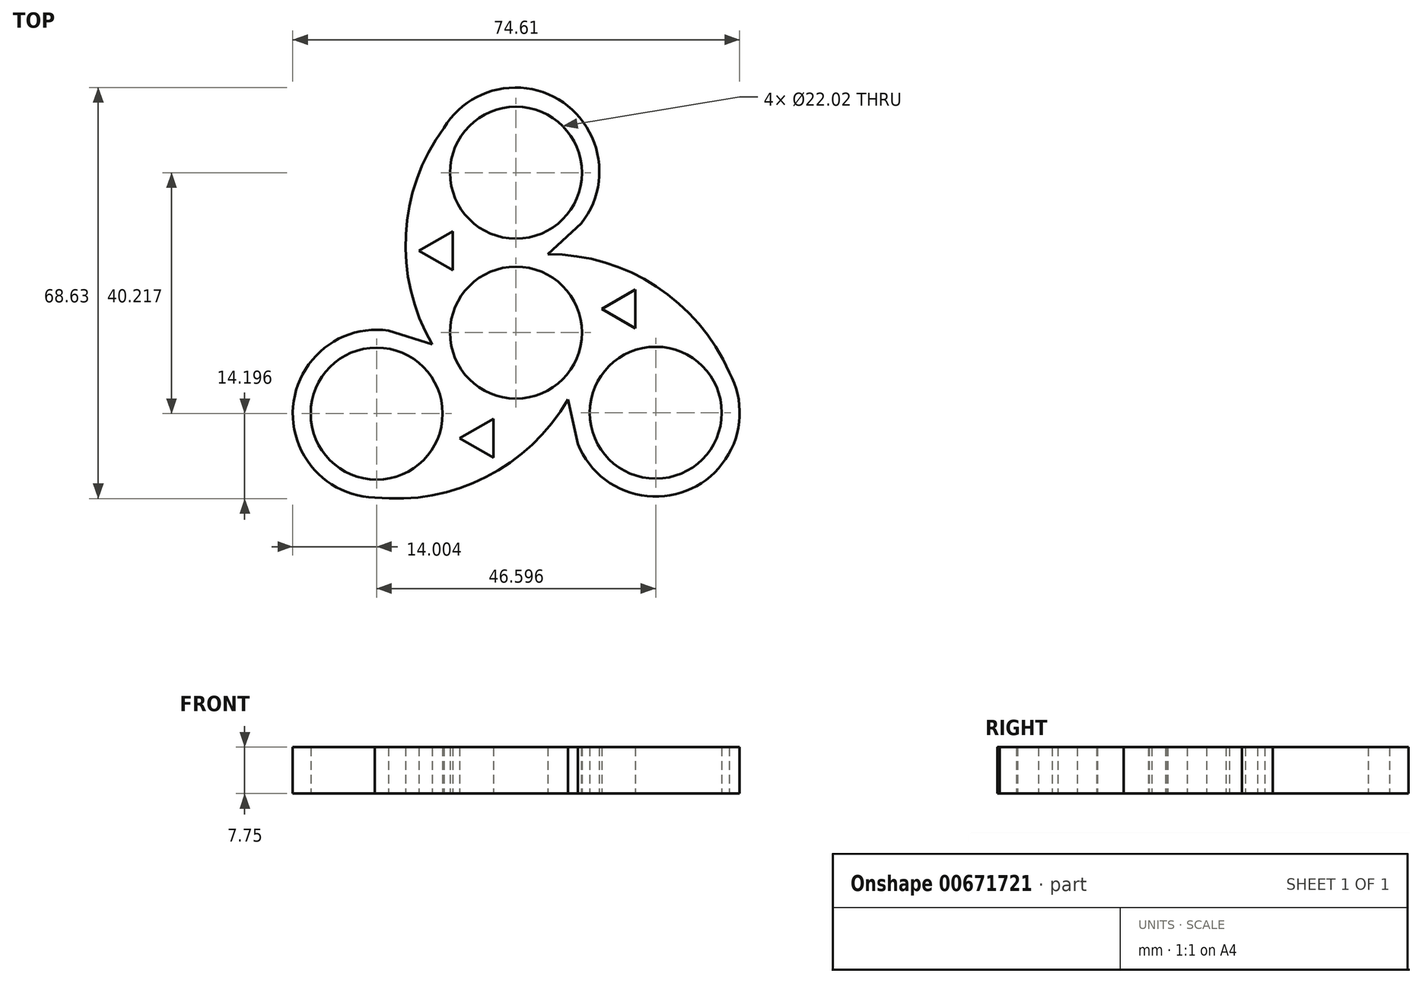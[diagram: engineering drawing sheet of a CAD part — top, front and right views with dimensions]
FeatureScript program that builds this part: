
annotation { "Feature Type Name" : "Feature", "Feature Type Description" : "" }
export const myFeature = defineFeature(function(context is Context, id is Id, definition is map)
    precondition{}
    {
        {
            var Q0;
            Q0=qCreatedBy(makeId("Top.planeOp"),FACE);
            var sketch = newSketch(context, id + "F0", { "sketchPlane" : qUnion([Q0])});
            skCircle(sketch, "E0", {"center": v(0, 0) * mm, "radius": 11.01 * mm});
            skCircle(sketch, "E1", {"center": v(0, 26.7) * mm, "radius": 11.01 * mm});
            skArc(sketch, "E2", {"start": v(10.93, 18.25) * mm, "mid": v(7.9, 38.4) * mm, "end": v(-12.04, 34.2) * mm});
            skPoint(sketch, "E3.end.orphan", {"position": v(-12.04, -10.58) * mm});
            skLineSegment(sketch, "E4", {"start": v(10.93, 18.25) * mm, "end": v(5.3, 13.1) * mm});
            skLineSegment(sketch, "E5.1.1", {"start": v(-21.27, 0.34) * mm, "end": v(-14, -1.95) * mm});
            skArc(sketch, "E5.1.2", {"start": v(-21.27, 0.34) * mm, "mid": v(-37.21, -12.36) * mm, "end": v(-23.6, -27.53) * mm});
            skLineSegment(sketch, "E5.2.1", {"start": v(10.34, -18.6) * mm, "end": v(8.69, -11.14) * mm});
            skArc(sketch, "E5.2.2", {"start": v(10.34, -18.6) * mm, "mid": v(29.31, -26.05) * mm, "end": v(35.63, -6.67) * mm});
            skPoint(sketch, "E6.start.orphan", {"position": v(13.04, 0) * mm});
            skArc(sketch, "E7", {"start": v(-23.6, -27.53) * mm, "mid": v(-5.01, -24.14) * mm, "end": v(8.69, -11.14) * mm});
            skArc(sketch, "E8.1.0", {"start": v(35.63, -6.67) * mm, "mid": v(23.4, 7.72) * mm, "end": v(5.3, 13.1) * mm});
            skArc(sketch, "E8.2.0", {"start": v(-12.04, 34.2) * mm, "mid": v(-18.4, 16.41) * mm, "end": v(-14, -1.95) * mm});
            skCircle(sketch, "E9", {"center": v(23.34, -13.38) * mm, "radius": 11.01 * mm});
            skCircle(sketch, "E10", {"center": v(-23.26, -13.52) * mm, "radius": 11.01 * mm});
            skLineSegment(sketch, "E11.0", {"start": v(-10.57, 16.93) * mm, "end": v(-10.57, 10.44) * mm});
            skLineSegment(sketch, "E11.1", {"start": v(-10.57, 10.44) * mm, "end": v(-16.2, 13.69) * mm});
            skLineSegment(sketch, "E11.2", {"start": v(-16.2, 13.69) * mm, "end": v(-10.57, 16.93) * mm});
            skPoint(sketch, "E11.0.midPoint", {"position": v(-10.57, 13.69) * mm});
            skLineSegment(sketch, "E12.1.0", {"start": v(-3.76, -20.87) * mm, "end": v(-9.38, -17.62) * mm});
            skLineSegment(sketch, "E12.1.1", {"start": v(-9.38, -17.62) * mm, "end": v(-3.76, -14.38) * mm});
            skLineSegment(sketch, "E12.1.2", {"start": v(-3.76, -14.38) * mm, "end": v(-3.76, -20.87) * mm});
            skLineSegment(sketch, "E12.2.0", {"start": v(19.95, 7.18) * mm, "end": v(19.95, 0.69) * mm});
            skLineSegment(sketch, "E12.2.1", {"start": v(19.95, 0.69) * mm, "end": v(14.33, 3.94) * mm});
            skLineSegment(sketch, "E12.2.2", {"start": v(14.33, 3.94) * mm, "end": v(19.95, 7.18) * mm});
            skSolve(sketch);
        }
        {
            var Q0;
            Q0 = qSketchRegion(id + "F0", true);
            extrude(context, id + "F1", {"entities" : qUnion([Q0]), "depth" : 7.75 * mm, "offsetDistance" : 25.4 * mm});
        }
    });
